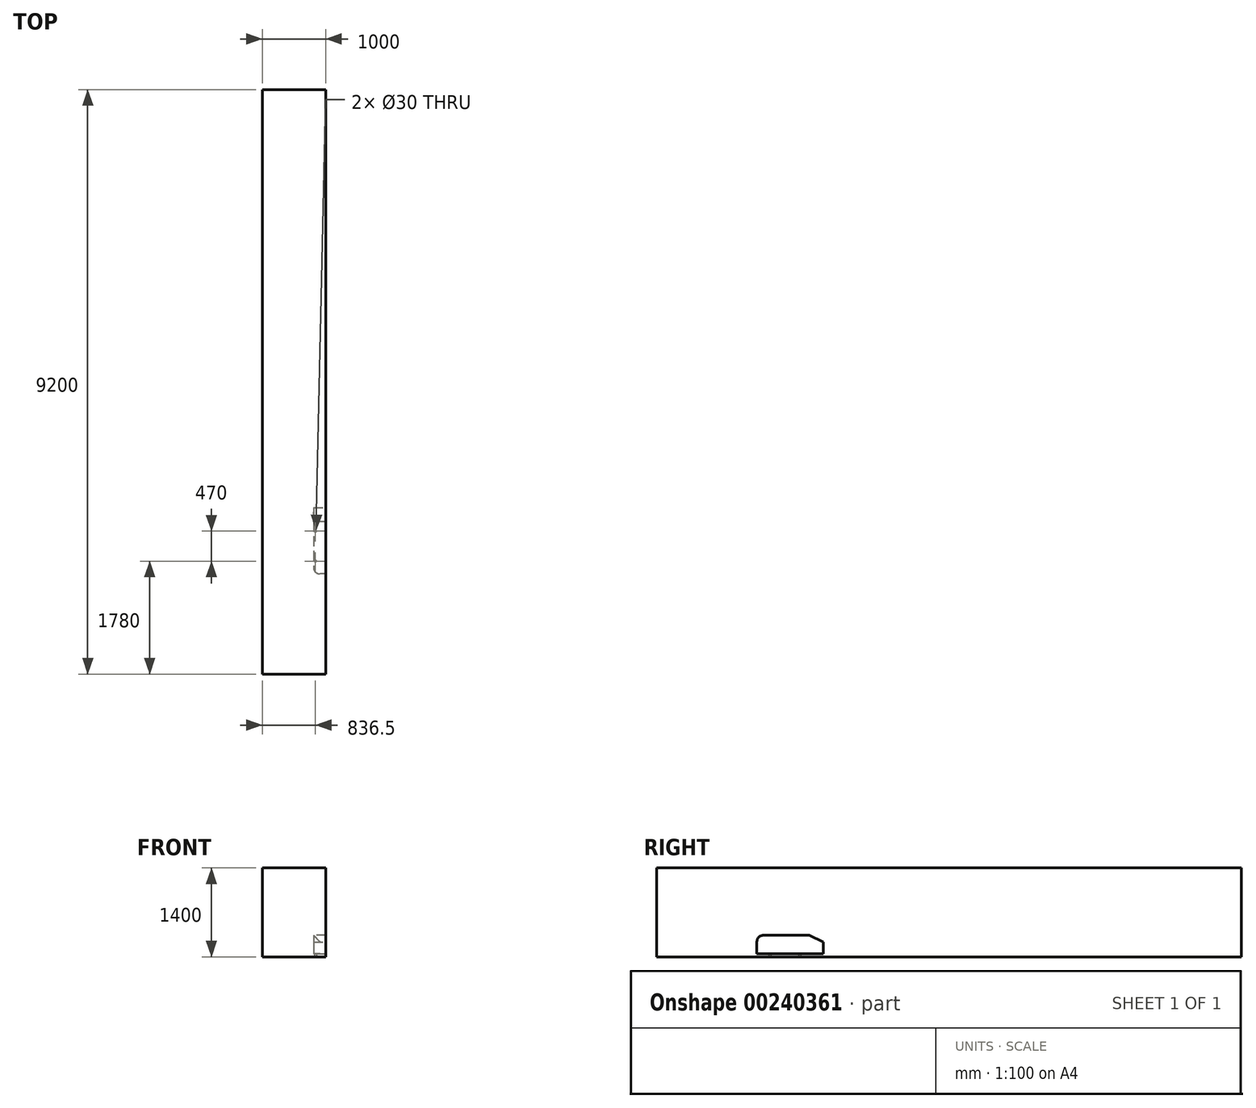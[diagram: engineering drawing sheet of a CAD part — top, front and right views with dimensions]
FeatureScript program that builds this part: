
annotation { "Feature Type Name" : "Feature", "Feature Type Description" : "" }
export const myFeature = defineFeature(function(context is Context, id is Id, definition is map)
    precondition{}
    {
        {
            var Q0;
            Q0=qCreatedBy(makeId("Top.planeOp"),FACE);
            var sketch = newSketch(context, id + "F0", { "sketchPlane" : qUnion([Q0])});
            skLineSegment(sketch, "E0.bottom", {"start": v(192, 522) * mm, "end": v(-192, 522) * mm});
            skLineSegment(sketch, "E0.top", {"start": v(192, -522) * mm, "end": v(-192, -522) * mm});
            skLineSegment(sketch, "E0.left", {"start": v(192, 522) * mm, "end": v(192, -522) * mm});
            skLineSegment(sketch, "E0.right", {"start": v(-192, 522) * mm, "end": v(-192, -522) * mm});
            skPoint(sketch, "E0.middle", {"position": v(0, 0) * mm});
            skSolve(sketch);
        }
        {
            var Q0;
            Q0 = qSketchRegion(id + "F0", true);
            extrude(context, id + "F1", {"entities" : qUnion([Q0]), "depth" : 338 * mm});
        }
        {
            var Q0;
            Q0=makeQuery(id+"F1.opExtrude","SWEPT_FACE",FACE,{"disambiguationData":[OSD([sQuery(id+"F0.wireOp",EDGE,"E0.top")])]});
            var sketch = newSketch(context, id + "F2", { "sketchPlane" : qUnion([Q0])});
            skLineSegment(sketch, "E1.bottom", {"start": v(-192, 0) * mm, "end": v(192, 0) * mm});
            skLineSegment(sketch, "E1.top", {"start": v(-192, 50) * mm, "end": v(192, 50) * mm});
            skLineSegment(sketch, "E1.left", {"start": v(-192, 0) * mm, "end": v(-192, 50) * mm});
            skLineSegment(sketch, "E1.right", {"start": v(192, 0) * mm, "end": v(192, 50) * mm});
            skSolve(sketch);
        }
        {
            var Q0;
            Q0 = qSketchRegion(id + "F2", true);
            extrude(context, id + "F3", {"entities" : qUnion([Q0]), "operationType" : NewBodyOperationType.REMOVE, "endBound" : BoundingType.THROUGH_ALL, "oppositeDirection" : true, "depth" : 25 * mm});
        }
        {
            var Q0;
            Q0=makeQuery(id+"F1.opExtrude","SWEPT_EDGE",EDGE,{"disambiguationData":[OSD([sQuery(id+"F0.wireOp",EDGE,"E0.top"),sQuery(id+"F0.wireOp",EDGE,"E0.right")])]});
            var Q1;
            Q1=makeQuery(id+"F1.opExtrude","CAP_EDGE",EDGE,{"disambiguationData":[OSD([sQuery(id+"F0.wireOp",EDGE,"E0.top")])],"isStart":false});
            var Q2;
            Q2=makeQuery(id+"F1.opExtrude","SWEPT_EDGE",EDGE,{"disambiguationData":[OSD([sQuery(id+"F0.wireOp",EDGE,"E0.top"),sQuery(id+"F0.wireOp",EDGE,"E0.left")])]});
            var Q3;
            Q3=makeQuery(id+"F3.boolean.opBoolean","COPY",EDGE,{"derivedFrom":makeQuery(id+"F3.opExtrude","CAP_EDGE",EDGE,{"disambiguationData":[OSD([sQuery(id+"F2.wireOp",EDGE,"E1.top")])],"isStart":true})});
            fillet(context, id + "F4", {"entities" : qUnion([Q0, Q1, Q2, Q3]), "radius" : 100 * mm, "tangentPropagation" : true, "allowEdgeOverflow" : false});
        }
        {
            var Q0;
            Q0=makeQuery(id+"F1.opExtrude","CAP_EDGE",EDGE,{"disambiguationData":[OSD([sQuery(id+"F0.wireOp",EDGE,"E0.bottom")])],"isStart":false});
            chamfer(context, id + "F5", {"entities" : qUnion([Q0]), "chamferType" : ChamferType.OFFSET_ANGLE, "width" : 222 * mm, "oppositeDirection" : false, "angle" : 25 * degree, "tangentPropagation" : true});
        }
        {
            var Q0;
            Q0=qCreatedBy(makeId("Top.planeOp"),FACE);
            var sketch = newSketch(context, id + "F6", { "sketchPlane" : qUnion([Q0])});
            skCircle(sketch, "E2", {"center": v(163.5, -320) * mm, "radius": 15 * mm});
            skCircle(sketch, "E3", {"center": v(163.5, 150) * mm, "radius": 15 * mm});
            skCircle(sketch, "E4", {"center": v(-163.5, 150) * mm, "radius": 15 * mm});
            skCircle(sketch, "E5", {"center": v(-163.5, -320) * mm, "radius": 15 * mm});
            skSolve(sketch);
        }
        {
            var Q0;
            Q0 = qSketchRegion(id + "F6", true);
            extrude(context, id + "F7", {"entities" : qUnion([Q0]), "operationType" : NewBodyOperationType.ADD, "endBound" : BoundingType.UP_TO_NEXT, "depth" : 25 * mm});
        }
        {
            var Q0;
            Q0=qCreatedBy(makeId("Top.planeOp"),FACE);
            var sketch = newSketch(context, id + "F8", { "sketchPlane" : qUnion([Q0])});
            skLineSegment(sketch, "E6.bottom", {"start": v(-1000, 7100) * mm, "end": v(1000, 7100) * mm});
            skLineSegment(sketch, "E6.top", {"start": v(-1000, -2100) * mm, "end": v(1000, -2100) * mm});
            skLineSegment(sketch, "E6.left", {"start": v(-1000, 7100) * mm, "end": v(-1000, -2100) * mm});
            skLineSegment(sketch, "E6.right", {"start": v(1000, 7100) * mm, "end": v(1000, -2100) * mm});
            skSolve(sketch);
        }
        {
            var Q0;
            Q0 = qSketchRegion(id + "F8", true);
            extrude(context, id + "F9", {"entities" : qUnion([Q0]), "depth" : 1400 * mm});
        }
        {
            var Q0;
            Q0=makeQuery(id+"F1.opExtrude","SWEPT_BODY",BODY,{"disambiguationData":[OSD([sQuery(id+"F0.wireOp",EDGE,"E0.bottom"),sQuery(id+"F0.wireOp",EDGE,"E0.top"),sQuery(id+"F0.wireOp",EDGE,"E0.left"),sQuery(id+"F0.wireOp",EDGE,"E0.right")])]});
            var Q1;
            Q1=makeQuery(id+"F9.opExtrude","SWEPT_BODY",BODY,{"disambiguationData":[OSD([sQuery(id+"F8.wireOp",EDGE,"E6.bottom"),sQuery(id+"F8.wireOp",EDGE,"E6.top"),sQuery(id+"F8.wireOp",EDGE,"E6.left"),sQuery(id+"F8.wireOp",EDGE,"E6.right")])]});
            booleanBodies(context, id + "F10", {"operationType" : BooleanOperationType.SUBTRACTION, "tools" : qUnion([Q0]), "targets" : qUnion([Q1])});
        }
        {
            var Q0;
            Q0=makeQuery(id+"F9.opExtrude","SWEPT_FACE",FACE,{"disambiguationData":[OSD([sQuery(id+"F8.wireOp",EDGE,"E6.top")])]});
            var sketch = newSketch(context, id + "F11", { "sketchPlane" : qUnion([Q0])});
            skLineSegment(sketch, "E7.bottom", {"start": v(1000, 1400) * mm, "end": v(0, 1400) * mm});
            skLineSegment(sketch, "E7.top", {"start": v(1000, 0) * mm, "end": v(0, 0) * mm});
            skLineSegment(sketch, "E7.left", {"start": v(1000, 1400) * mm, "end": v(1000, 0) * mm});
            skLineSegment(sketch, "E7.right", {"start": v(0, 1400) * mm, "end": v(0, 0) * mm});
            skSolve(sketch);
        }
        {
            var Q0;
            Q0=makeQuery(id+"F11.imprint","IMPRINT",FACE,{"disambiguationData":[TD([[makeQuery(id+"F11.imprint","IMPRINT",EDGE,{"derivedFrom":sQuery(id+"F11.wireOp",EDGE,"E7.bottom")}),-1.0]])]});
            extrude(context, id + "F12", {"entities" : qUnion([Q0]), "operationType" : NewBodyOperationType.REMOVE, "endBound" : BoundingType.THROUGH_ALL, "oppositeDirection" : true, "depth" : 25 * mm});
        }
    });
